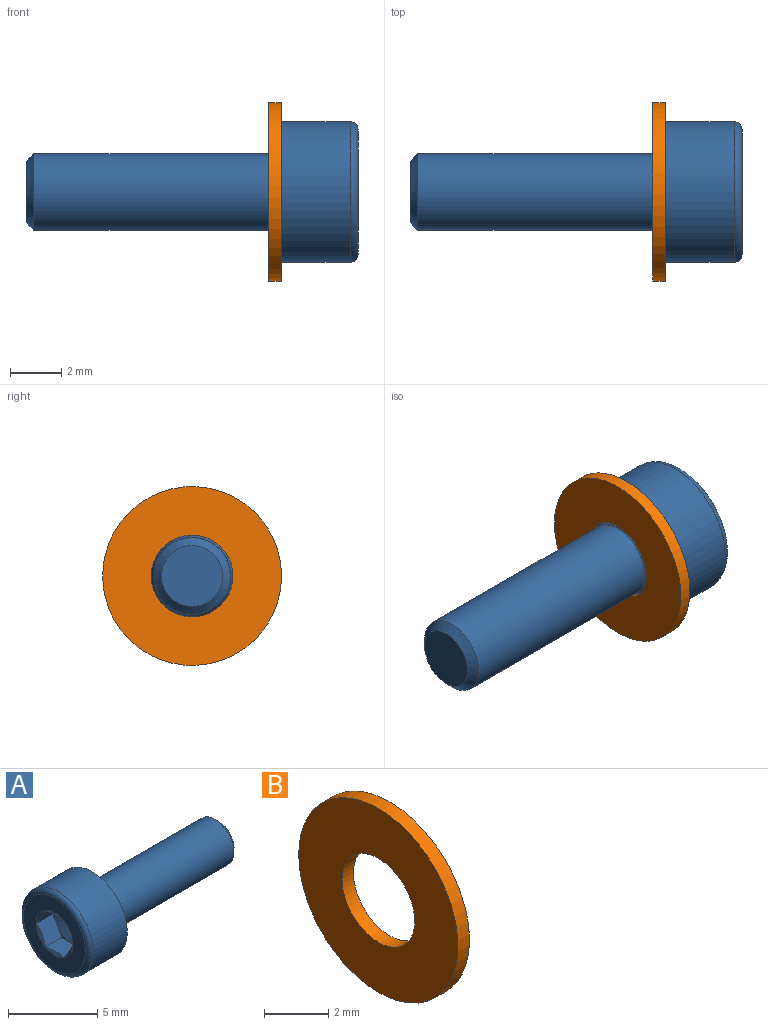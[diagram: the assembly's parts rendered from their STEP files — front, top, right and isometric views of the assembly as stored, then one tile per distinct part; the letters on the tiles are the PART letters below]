
ASSEMBLY  parts=2 mates=1
PART A: 24 faces, bbox 13x6x6 mm
  f0: plane 1.08x0.63mm, normal (-1,0,0), area 0.1mm2, adj f16,f17,f23
  f1: plane 1.25x0.36mm, normal (-1,0,0), area 0.1mm2, adj f17,f18,f23
  f2: plane 1.08x0.63mm, normal (-1,0,0), area 0.1mm2, adj f18,f19,f23
  f3: plane 1.08x0.63mm, normal (-1,0,0), area 0.1mm2, adj f19,f20,f23
  f4: plane 1.25x0.36mm, normal (-1,0,0), area 0.1mm2, adj f20,f21,f23
  f5: cone r=1.45mm half-angle=60deg, axis (-1,0,0), area 1.4mm2, adj f15,f16,f17,f18,f19,f20,f21
  f6: cone r=1.51mm half-angle=26deg, axis (-1,0,0), area 4.6mm2, adj f7,f11
  f7: torus R=1.6mm, axis (1,0,0), area 0.4mm2, adj f6,f10
  f8: plane 2.39x2.39mm, normal (1,0,0), area 4.5mm2, adj f9
  f9: cone r=1.5mm half-angle=45deg, axis (-1,0,0), area 3.7mm2, adj f8,f10
  f10: cylinder r=1.5mm len=9.18mm, axis (1,0,0), area 86.6mm2, adj f7,f9
  f11: torus R=1.8mm, axis (1,0,0), area 1.2mm2, adj f6,f13
  f12: cylinder r=2.75mm len=5.5mm, axis (1,0,0), area 46.7mm2, adj f13,f14
  f13: plane 5.5x5.5mm, normal (1,0,0), area 13.6mm2, adj f11,f12
  f14: torus R=2.45mm, axis (1,0,0), area 7.8mm2, adj f12,f15
  f15: plane 4.9x4.9mm, normal (-1,0,0), area 12.2mm2, adj f5,f14
  f16: plane 1.45x1.3mm, normal (0,0,-1), area 1.8mm2, adj f0,f5,f17,f21,f22
  f17: plane 1.29x1.25mm, normal (0,0.87,-0.5), area 1.8mm2, adj f0,f1,f5,f16,f18
  f18: plane 1.29x1.25mm, normal (0,0.87,0.5), area 1.8mm2, adj f1,f2,f5,f17,f19
  f19: plane 1.45x1.3mm, normal (0,0,1), area 1.8mm2, adj f2,f3,f5,f18,f20
  f20: plane 1.29x1.25mm, normal (0,-0.87,0.5), area 1.8mm2, adj f3,f4,f5,f19,f21
  f21: plane 1.29x1.25mm, normal (0,-0.87,-0.5), area 1.8mm2, adj f4,f5,f16,f20,f22
  f22: plane 1.08x0.63mm, normal (-1,0,0), area 0.1mm2, adj f16,f21,f23
  f23: cone r=1.25mm half-angle=60deg, axis (-1,0,0), area 5.7mm2, adj f0,f1,f2,f3,f4,f22
PART B: 4 faces, bbox 0.5x7x7 mm
  f0: plane 7x7mm, normal (-1,0,0), area 30.4mm2, adj f1,f3
  f1: cylinder r=1.6mm len=3.2mm, axis (1,0,0), area 5mm2, adj f0,f2
  f2: plane 7x7mm, normal (1,0,0), area 30.4mm2, adj f1,f3
  f3: cylinder r=3.5mm len=7mm, axis (1,0,0), area 11mm2, adj f0,f2
PLACE A rot(axis=(0,1,0),180deg) t=(0.5,0,0)mm
PLACE B at identity fixed
MATE fastened A.f5 <-> B.f1  axis (-1,0,0) through (0.5,0,0)mm
